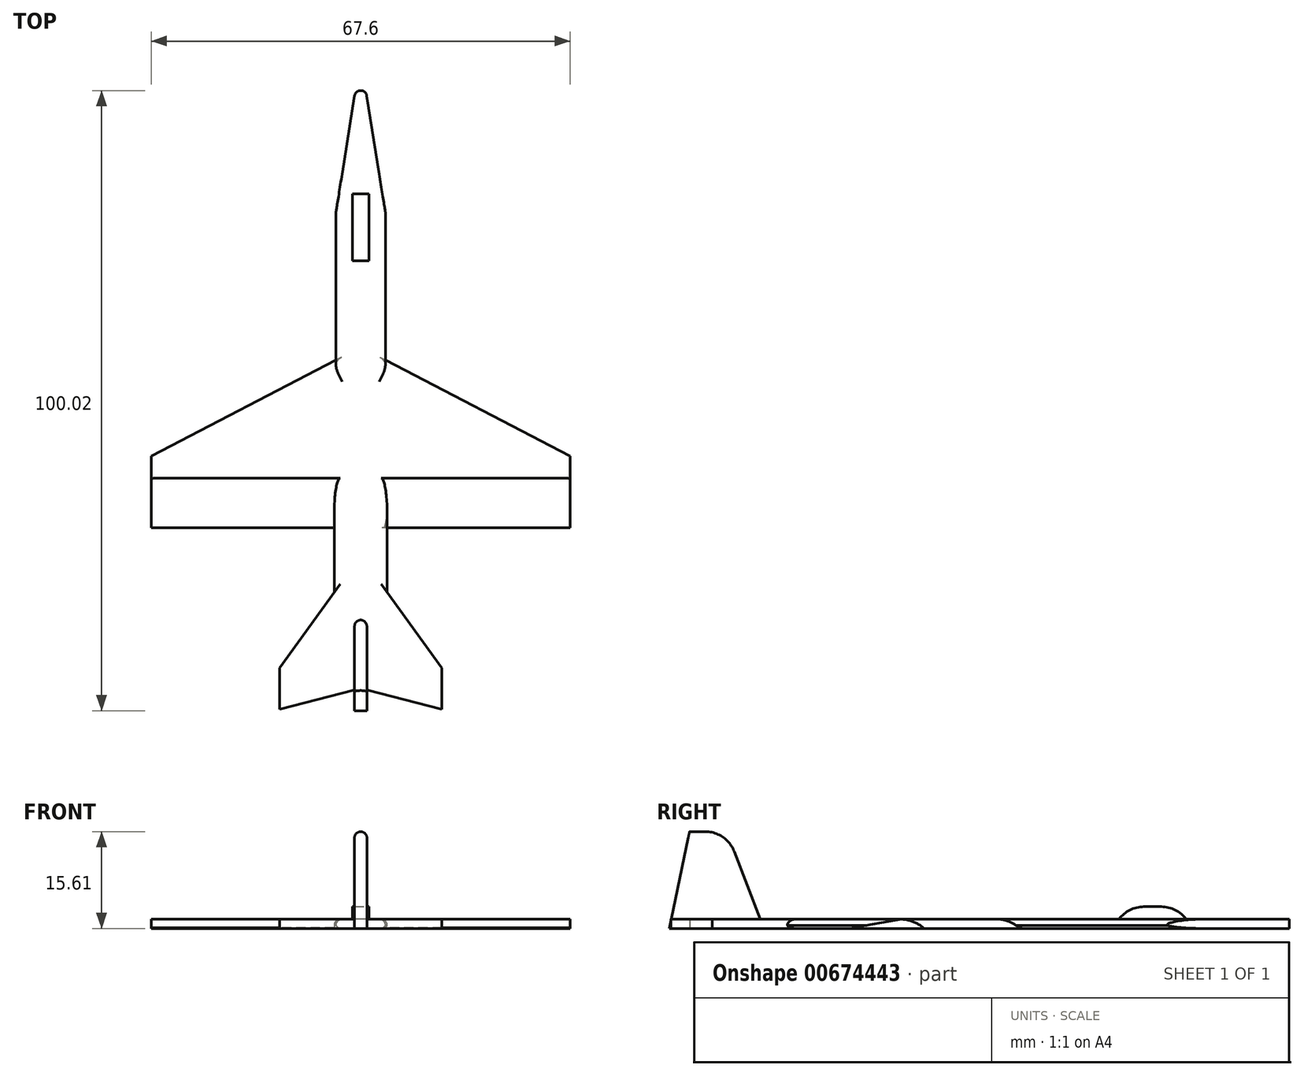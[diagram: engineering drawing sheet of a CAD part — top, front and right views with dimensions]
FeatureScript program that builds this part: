
annotation { "Feature Type Name" : "Feature", "Feature Type Description" : "" }
export const myFeature = defineFeature(function(context is Context, id is Id, definition is map)
    precondition{}
    {
        {
            var Q0;
            Q0=qCreatedBy(makeId("Top.planeOp"),FACE);
            var sketch = newSketch(context, id + "F0", { "sketchPlane" : qUnion([Q0])});
            skLineSegment(sketch, "E0", {"start": v(0, 35.73) * mm, "end": v(-4, 10.62) * mm});
            skLineSegment(sketch, "E1", {"start": v(-4, 10.62) * mm, "end": v(-4, -13.1) * mm});
            skLineSegment(sketch, "E2", {"start": v(-4, -13.1) * mm, "end": v(-33.8, -28.56) * mm});
            skLineSegment(sketch, "E3", {"start": v(-33.8, -28.56) * mm, "end": v(-33.8, -40.14) * mm});
            skLineSegment(sketch, "E4", {"start": v(-33.8, -40.14) * mm, "end": v(-4.28, -40.14) * mm});
            skLineSegment(sketch, "E5", {"start": v(-4.28, -40.14) * mm, "end": v(-4.28, -50.63) * mm});
            skLineSegment(sketch, "E6", {"start": v(-4.28, -50.63) * mm, "end": v(-13.1, -62.77) * mm});
            skLineSegment(sketch, "E7", {"start": v(-13.1, -62.77) * mm, "end": v(-13.1, -69.39) * mm});
            skLineSegment(sketch, "E8", {"start": v(-13.1, -69.39) * mm, "end": v(0, -66.08) * mm});
            skLineSegment(sketch, "E9", {"start": v(0, -66.08) * mm, "end": v(0, 35.73) * mm});
            skSolve(sketch);
        }
        {
            var Q0;
            Q0 = qSketchRegion(id + "F0", true);
            extrude(context, id + "F1", {"entities" : qUnion([Q0]), "depth" : 1.5 * mm, "offsetDistance" : 25.4 * mm});
        }
        {
            var Q0;
            Q0=makeQuery(id+"F1.opExtrude","CAP_FACE",FACE,{"disambiguationData":[OSD([sQuery(id+"F0.wireOp",EDGE,"E0"),sQuery(id+"F0.wireOp",EDGE,"E1"),sQuery(id+"F0.wireOp",EDGE,"E2"),sQuery(id+"F0.wireOp",EDGE,"E3"),sQuery(id+"F0.wireOp",EDGE,"E4"),sQuery(id+"F0.wireOp",EDGE,"E5"),sQuery(id+"F0.wireOp",EDGE,"E6"),sQuery(id+"F0.wireOp",EDGE,"E7"),sQuery(id+"F0.wireOp",EDGE,"E8"),sQuery(id+"F0.wireOp",EDGE,"E9")])],"isStart":false});
            var sketch = newSketch(context, id + "F2", { "sketchPlane" : qUnion([Q0])});
            skLineSegment(sketch, "E10.bottom", {"start": v(0, 13.73) * mm, "end": v(-1.35, 13.73) * mm});
            skLineSegment(sketch, "E10.top", {"start": v(0, 2.88) * mm, "end": v(-1.35, 2.88) * mm});
            skLineSegment(sketch, "E10.left", {"start": v(0, 13.73) * mm, "end": v(0, 2.88) * mm});
            skLineSegment(sketch, "E10.right", {"start": v(-1.35, 13.73) * mm, "end": v(-1.35, 2.88) * mm});
            skSolve(sketch);
        }
        {
            var Q0;
            Q0 = qSketchRegion(id + "F2", true);
            extrude(context, id + "F3", {"entities" : qUnion([Q0]), "operationType" : NewBodyOperationType.ADD, "depth" : 2 * mm, "offsetDistance" : 25 * mm});
        }
        {
            var Q0;
            Q0=qCreatedBy(makeId("Right.planeOp"),FACE);
            var sketch = newSketch(context, id + "F4", { "sketchPlane" : qUnion([Q0])});
            skLineSegment(sketch, "E11", {"start": v(-54.45, 0) * mm, "end": v(-59.2, 12.4) * mm});
            skLineSegment(sketch, "E12", {"start": v(-63.86, 15.61) * mm, "end": v(-66.4, 15.61) * mm});
            skLineSegment(sketch, "E13", {"start": v(-66.4, 15.61) * mm, "end": v(-69.65, 0) * mm});
            skLineSegment(sketch, "E14", {"start": v(-69.65, 0) * mm, "end": v(-54.45, 0) * mm});
            skPoint(sketch, "E15.visualSharp", {"position": v(-60.42, 15.61) * mm});
            skArc(sketch, "E15.filletArc", {"start": v(-59.2, 12.4) * mm, "mid": v(-61.03, 14.73) * mm, "end": v(-63.86, 15.61) * mm});
            skSolve(sketch);
        }
        {
            var Q0;
            Q0 = qSketchRegion(id + "F4", true);
            extrude(context, id + "F5", {"entities" : qUnion([Q0]), "operationType" : NewBodyOperationType.ADD, "depth" : -1 * mm, "offsetDistance" : 25 * mm});
        }
        {
            var Q0;
            Q0=makeQuery(id+"F1.opExtrude","SWEPT_BODY",BODY,{"disambiguationData":[OSD([sQuery(id+"F0.wireOp",EDGE,"E0"),sQuery(id+"F0.wireOp",EDGE,"E1"),sQuery(id+"F0.wireOp",EDGE,"E2"),sQuery(id+"F0.wireOp",EDGE,"E3"),sQuery(id+"F0.wireOp",EDGE,"E4"),sQuery(id+"F0.wireOp",EDGE,"E5"),sQuery(id+"F0.wireOp",EDGE,"E6"),sQuery(id+"F0.wireOp",EDGE,"E7"),sQuery(id+"F0.wireOp",EDGE,"E8"),sQuery(id+"F0.wireOp",EDGE,"E9")])]});
            var Q1;
            Q1=makeQuery(id+"F5.boolean.opBoolean","MERGE",FACE,{"derivedFrom":[makeQuery(id+"F3.boolean.opBoolean","MERGE",FACE,{"derivedFrom":[makeQuery(id+"F1.opExtrude","SWEPT_FACE",FACE,{"disambiguationData":[OSD([sQuery(id+"F0.wireOp",EDGE,"E9")])]}),makeQuery(id+"F3.opExtrude","SWEPT_FACE",FACE,{"disambiguationData":[OSD([sQuery(id+"F2.wireOp",EDGE,"E10.left")])]})]}),makeQuery(id+"F5.opExtrude","CAP_FACE",FACE,{"disambiguationData":[OSD([sQuery(id+"F4.wireOp",EDGE,"E11"),sQuery(id+"F4.wireOp",EDGE,"E12"),sQuery(id+"F4.wireOp",EDGE,"E13"),sQuery(id+"F4.wireOp",EDGE,"E14"),sQuery(id+"F4.wireOp",EDGE,"E15.filletArc")])],"isStart":true})]});
            mirror(context, id + "F6", {"operationType" : NewBodyOperationType.ADD, "entities" : qUnion([Q0]), "mirrorPlane" : qUnion([Q1])});
        }
        {
            var Q0;
            Q0=makeQuery(id+"F1.opExtrude","CAP_EDGE",EDGE,{"disambiguationData":[OSD([sQuery(id+"F0.wireOp",EDGE,"E2")])],"isStart":false});
            var Q1;
            Q1=makeQuery(id+"F6.opPattern","COPY",EDGE,{"derivedFrom":makeQuery(id+"F1.opExtrude","CAP_EDGE",EDGE,{"disambiguationData":[OSD([sQuery(id+"F0.wireOp",EDGE,"E2")])],"isStart":false}),"instanceName":"1"});
            fillet(context, id + "F7", {"entities" : qUnion([Q0, Q1]), "radius" : 5 * mm, "tangentPropagation" : true, "allowEdgeOverflow" : false});
        }
        {
            var Q0;
            {var subQ0=makeQuery(id+"F3.opExtrude","CAP_EDGE",EDGE,{"disambiguationData":[OSD([sQuery(id+"F2.wireOp",EDGE,"E10.bottom")])],"isStart":false});Q0=makeQuery(id+"F6.boolean.opBoolean","MERGE",EDGE,{"derivedFrom":[subQ0,makeQuery(id+"F6.opPattern","COPY",EDGE,{"derivedFrom":subQ0,"instanceName":"1"})]});}
            fillet(context, id + "F8", {"entities" : qUnion([Q0]), "radius" : 5 * mm, "tangentPropagation" : true, "allowEdgeOverflow" : false});
        }
        {
            var Q0;
            {var subQ0=makeQuery(id+"F3.opExtrude","CAP_EDGE",EDGE,{"disambiguationData":[OSD([sQuery(id+"F2.wireOp",EDGE,"E10.top")])],"isStart":false});Q0=makeQuery(id+"F6.boolean.opBoolean","MERGE",EDGE,{"derivedFrom":[subQ0,makeQuery(id+"F6.opPattern","COPY",EDGE,{"derivedFrom":subQ0,"instanceName":"1"})]});}
            fillet(context, id + "F9", {"entities" : qUnion([Q0]), "radius" : 5 * mm, "tangentPropagation" : true, "allowEdgeOverflow" : false});
        }
        {
            var Q0;
            {var subQ0=makeQuery(id+"F1.opExtrude","SWEPT_EDGE",EDGE,{"disambiguationData":[OSD([sQuery(id+"F0.wireOp",EDGE,"E0"),sQuery(id+"F0.wireOp",EDGE,"E9")])]});Q0=makeQuery(id+"F6.boolean.opBoolean","MERGE",EDGE,{"derivedFrom":[subQ0,makeQuery(id+"F6.opPattern","COPY",EDGE,{"derivedFrom":subQ0,"instanceName":"1"})]});}
            fillet(context, id + "F10", {"entities" : qUnion([Q0]), "radius" : 1 * mm, "tangentPropagation" : true, "allowEdgeOverflow" : false});
        }
        {
            var Q0;
            Q0=makeQuery(id+"F1.opExtrude","CAP_EDGE",EDGE,{"disambiguationData":[OSD([sQuery(id+"F0.wireOp",EDGE,"E4")])],"isStart":false});
            var Q1;
            Q1=makeQuery(id+"F6.opPattern","COPY",EDGE,{"derivedFrom":makeQuery(id+"F1.opExtrude","CAP_EDGE",EDGE,{"disambiguationData":[OSD([sQuery(id+"F0.wireOp",EDGE,"E4")])],"isStart":false}),"instanceName":"1"});
            chamfer(context, id + "F11", {"entities" : qUnion([Q0, Q1]), "chamferType" : ChamferType.OFFSET_ANGLE, "width" : 8 * mm, "oppositeDirection" : false, "angle" : 10 * degree, "tangentPropagation" : true});
        }
        {
            var Q0;
            Q0=makeQuery(id+"F5.opExtrude","CAP_EDGE",EDGE,{"disambiguationData":[OSD([sQuery(id+"F4.wireOp",EDGE,"E11")])],"isStart":false});
            fillet(context, id + "F12", {"entities" : qUnion([Q0]), "radius" : 1 * mm, "tangentPropagation" : true, "allowEdgeOverflow" : false});
        }
        {
            var Q0;
            Q0=makeQuery(id+"F6.opPattern","COPY",EDGE,{"derivedFrom":makeQuery(id+"F5.opExtrude","CAP_EDGE",EDGE,{"disambiguationData":[OSD([sQuery(id+"F4.wireOp",EDGE,"E11")])],"isStart":false}),"instanceName":"1"});
            fillet(context, id + "F13", {"entities" : qUnion([Q0]), "radius" : 1 * mm, "tangentPropagation" : true, "allowEdgeOverflow" : false});
        }
        {
            var Q0;
            Q0=makeQuery(id+"F6.opPattern","COPY",EDGE,{"derivedFrom":makeQuery(id+"F1.opExtrude","CAP_EDGE",EDGE,{"disambiguationData":[OSD([sQuery(id+"F0.wireOp",EDGE,"E1")])],"isStart":false}),"instanceName":"1"});
            var Q1;
            Q1=makeQuery(id+"F1.opExtrude","CAP_EDGE",EDGE,{"disambiguationData":[OSD([sQuery(id+"F0.wireOp",EDGE,"E1")])],"isStart":false});
            var Q2;
            Q2=makeQuery(id+"F1.opExtrude","CAP_EDGE",EDGE,{"disambiguationData":[OSD([sQuery(id+"F0.wireOp",EDGE,"E5")])],"isStart":false});
            var Q3;
            Q3=makeQuery(id+"F6.opPattern","COPY",EDGE,{"derivedFrom":makeQuery(id+"F1.opExtrude","CAP_EDGE",EDGE,{"disambiguationData":[OSD([sQuery(id+"F0.wireOp",EDGE,"E5")])],"isStart":false}),"instanceName":"1"});
            fillet(context, id + "F14", {"entities" : qUnion([Q0, Q1, Q2, Q3]), "radius" : 1 * mm, "tangentPropagation" : true, "allowEdgeOverflow" : false});
        }
        {
            var Q0;
            Q0=makeQuery(id+"F6.opPattern","COPY",EDGE,{"derivedFrom":makeQuery(id+"F1.opExtrude","CAP_EDGE",EDGE,{"disambiguationData":[OSD([sQuery(id+"F0.wireOp",EDGE,"E1")])],"isStart":true}),"instanceName":"1"});
            var Q1;
            Q1=makeQuery(id+"F1.opExtrude","CAP_EDGE",EDGE,{"disambiguationData":[OSD([sQuery(id+"F0.wireOp",EDGE,"E1")])],"isStart":true});
            var Q2;
            Q2=makeQuery(id+"F6.opPattern","COPY",EDGE,{"derivedFrom":makeQuery(id+"F1.opExtrude","CAP_EDGE",EDGE,{"disambiguationData":[OSD([sQuery(id+"F0.wireOp",EDGE,"E5")])],"isStart":true}),"instanceName":"1"});
            fillet(context, id + "F15", {"entities" : qUnion([Q0, Q1, Q2]), "radius" : 1 * mm, "tangentPropagation" : true, "allowEdgeOverflow" : false});
        }
    });
